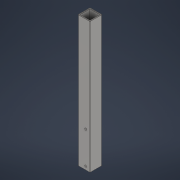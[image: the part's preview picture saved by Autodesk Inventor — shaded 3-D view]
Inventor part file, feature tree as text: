
AUTODESK INVENTOR PART (.ipt)
format: ipt  version: 2021 (Build 250183000, 183)  size: 165,376 bytes
history: native  units: mm
features: sketch x2, extrude x1, fillet x1, hole x1
ambient origin geometry x8: Origin, YZ Plane, XZ Plane, XY Plane, X Axis, Y Axis, Z Axis, Center Point
bodies: Solid1 (feature_tree)
feature tree (5):
  extrude  "Extrusion1"  Depth=50.0mm
  fillet  "Fillet1"  Radius=25.0mm
  hole  "Hole1"  [1 undecoded]
  sketch  "Sketch1"  dims[d0=50.0mm d1=50.0mm d2=25.0mm]
  sketch  "Sketch2"  dims[d3=25.0mm d4=5.0mm d5=539.0mm d6=0.0mm d7=2.0mm d12=8.0mm d13=6.0mm d14=4.0mm d15=2.0mm d16=90.0deg d17=8.0mm d18=20.594885mm d19=459.214mm d22=66.0mm d23=66.0mm d24=17.5mm d25=0.0mm]
note: 1 required parameter value undecoded (feature->parameter linkage not recoverable at this tier; creation-order binding heuristic only, values carry confidence <= 0.55)
